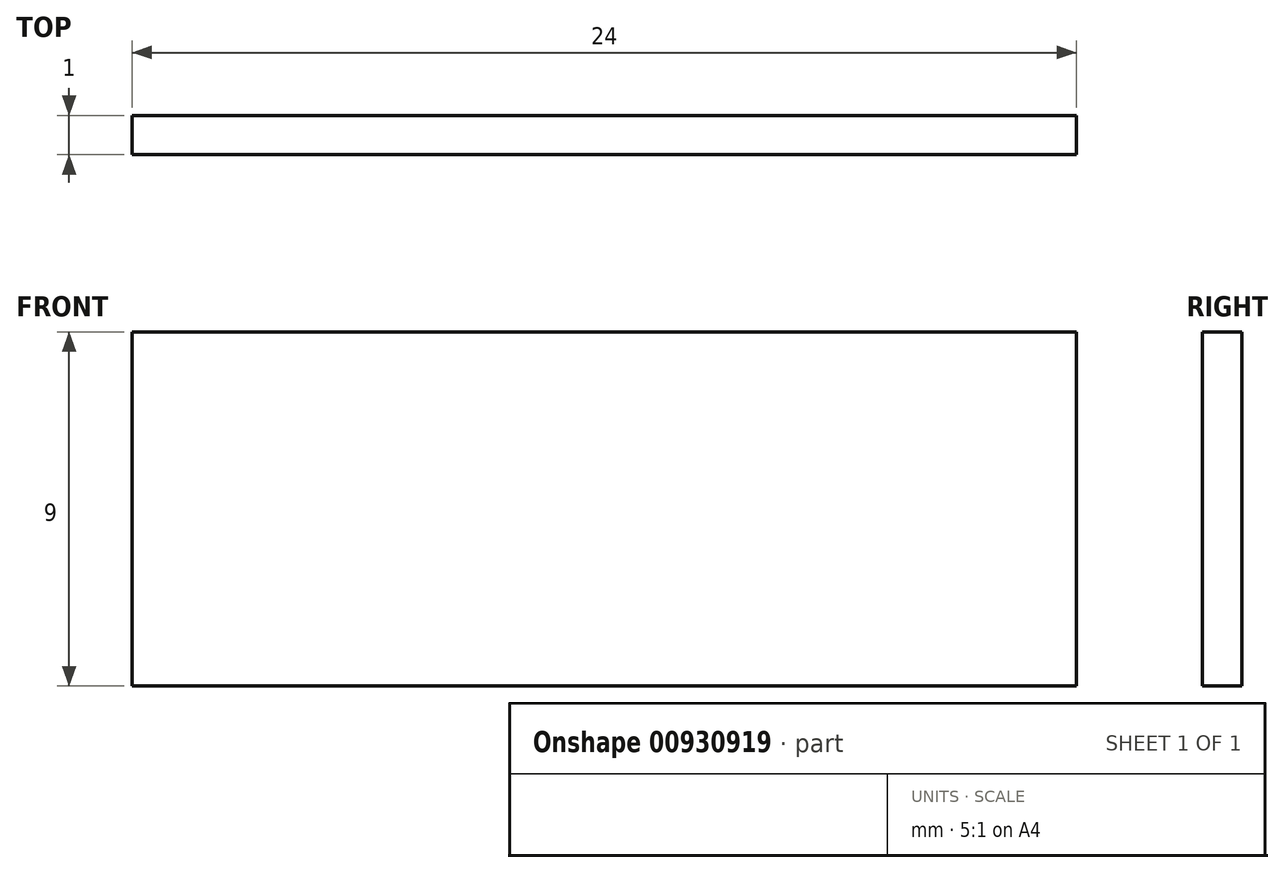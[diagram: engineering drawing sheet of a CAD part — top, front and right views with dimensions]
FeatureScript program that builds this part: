
annotation { "Feature Type Name" : "Feature", "Feature Type Description" : "" }
export const myFeature = defineFeature(function(context is Context, id is Id, definition is map)
    precondition{}
    {
        {
            var Q0;
            Q0=qCreatedBy(makeId("Front.planeOp"),FACE);
            var sketch = newSketch(context, id + "F0", { "sketchPlane" : qUnion([Q0])});
            skLineSegment(sketch, "E0.bottom", {"start": v(12, 4.5) * mm, "end": v(-12, 4.5) * mm});
            skLineSegment(sketch, "E0.top", {"start": v(12, -4.5) * mm, "end": v(-12, -4.5) * mm});
            skLineSegment(sketch, "E0.left", {"start": v(12, 4.5) * mm, "end": v(12, -4.5) * mm});
            skLineSegment(sketch, "E0.right", {"start": v(-12, 4.5) * mm, "end": v(-12, -4.5) * mm});
            skPoint(sketch, "E0.middle", {"position": v(0, 0) * mm});
            skSolve(sketch);
        }
        {
            var Q0;
            Q0=makeQuery(id+"F0.imprint","IMPRINT",FACE,{"disambiguationData":[TD([[makeQuery(id+"F0.imprint","IMPRINT",EDGE,{"derivedFrom":sQuery(id+"F0.wireOp",EDGE,"E0.bottom")}),1.0]])]});
            extrude(context, id + "F1", {"entities" : qUnion([Q0]), "depth" : 1 * mm, "offsetDistance" : 25 * mm});
        }
    });
